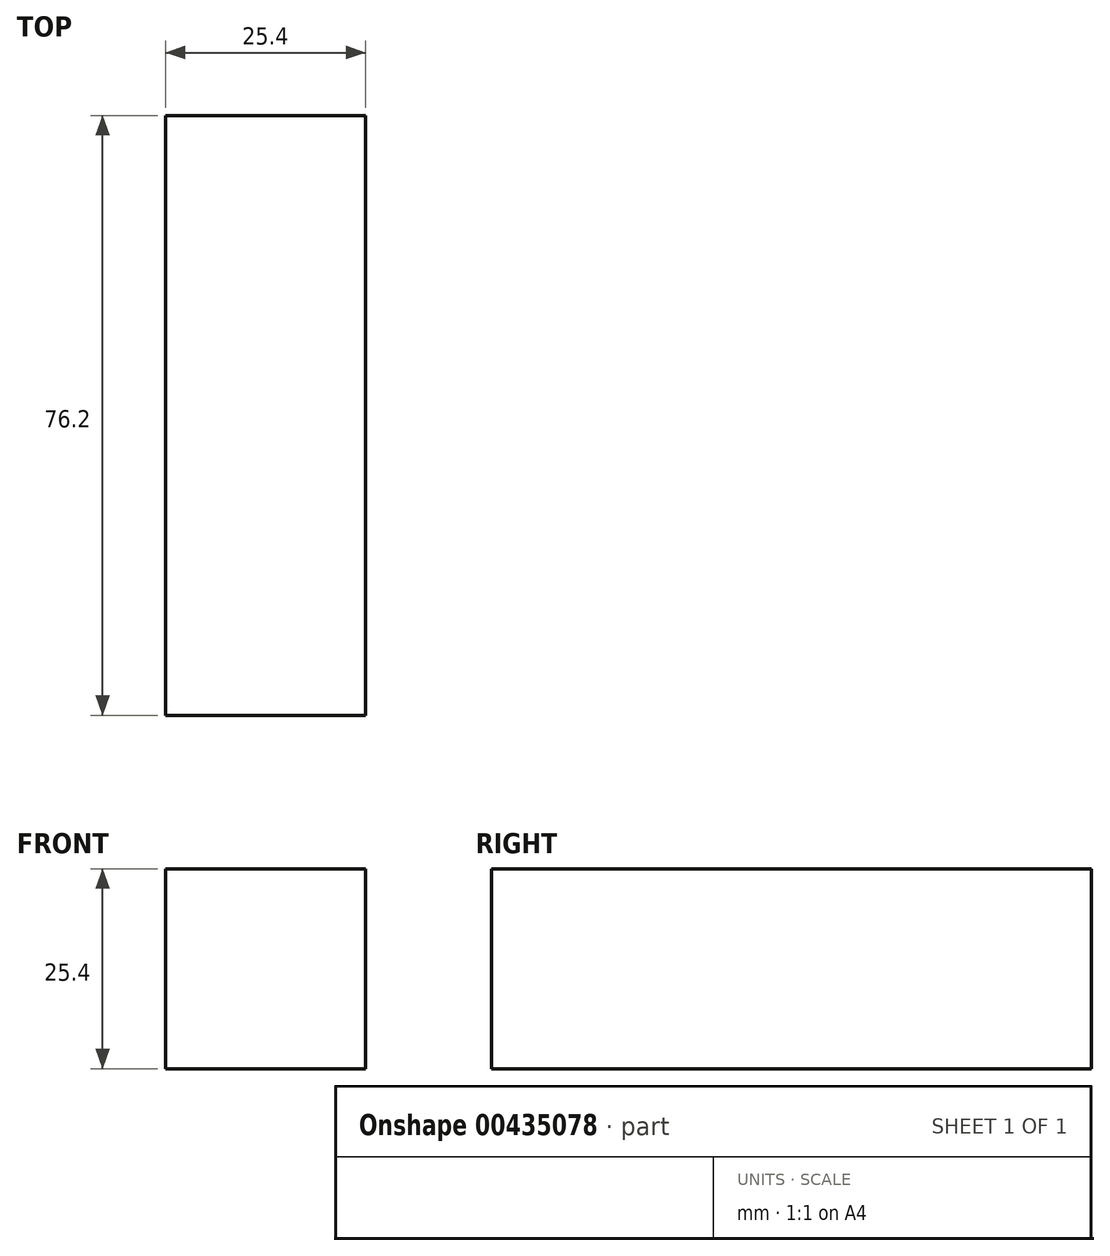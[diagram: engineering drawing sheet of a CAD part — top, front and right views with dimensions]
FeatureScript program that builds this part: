
annotation { "Feature Type Name" : "Feature", "Feature Type Description" : "" }
export const myFeature = defineFeature(function(context is Context, id is Id, definition is map)
    precondition{}
    {
        {
            var Q0;
            Q0=qCreatedBy(makeId("Front.planeOp"),FACE);
            var sketch = newSketch(context, id + "F0", { "sketchPlane" : qUnion([Q0])});
            skLineSegment(sketch, "E0.bottom", {"start": v(-6.2, 18.18) * mm, "end": v(-31.6, 18.18) * mm});
            skLineSegment(sketch, "E0.top", {"start": v(-6.2, 43.58) * mm, "end": v(-31.6, 43.58) * mm});
            skLineSegment(sketch, "E0.left", {"start": v(-6.2, 18.18) * mm, "end": v(-6.2, 43.58) * mm});
            skLineSegment(sketch, "E0.right", {"start": v(-31.6, 18.18) * mm, "end": v(-31.6, 43.58) * mm});
            skSolve(sketch);
        }
        {
            var Q0;
            Q0 = qSketchRegion(id + "F0", true);
            extrude(context, id + "F1", {"entities" : qUnion([Q0]), "depth" : 76.2 * mm});
        }
    });
